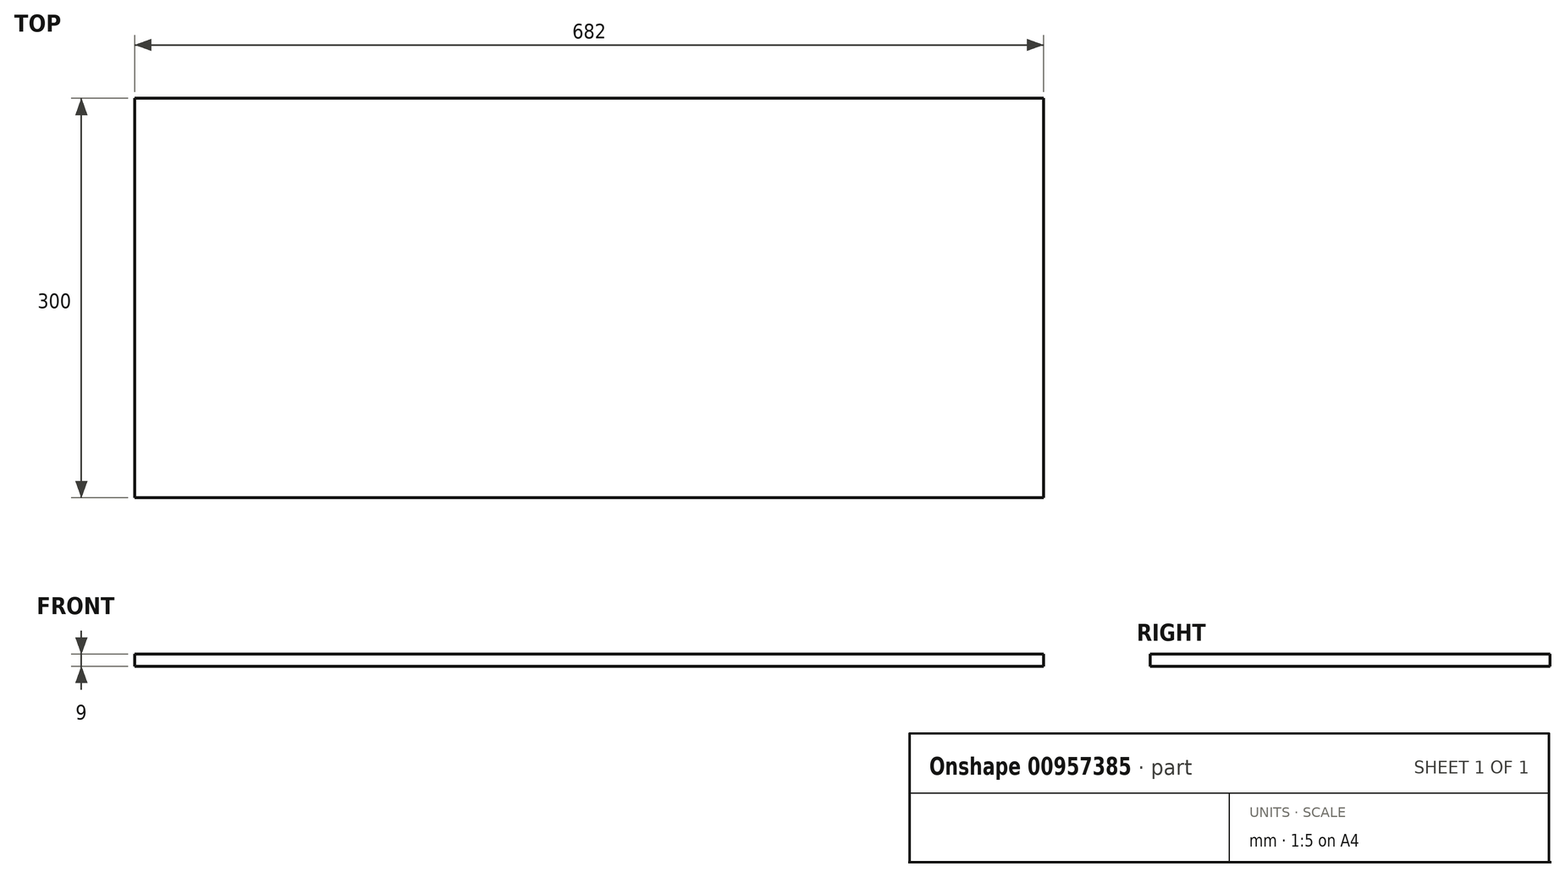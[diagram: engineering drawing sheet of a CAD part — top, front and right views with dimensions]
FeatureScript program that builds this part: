
annotation { "Feature Type Name" : "Feature", "Feature Type Description" : "" }
export const myFeature = defineFeature(function(context is Context, id is Id, definition is map)
    precondition{}
    {
        {
            var Q0;
            Q0=qCreatedBy(makeId("Top.planeOp"),FACE);
            var sketch = newSketch(context, id + "F0", { "sketchPlane" : qUnion([Q0])});
            skLineSegment(sketch, "E0.bottom", {"start": v(341, 150) * mm, "end": v(-341, 150) * mm});
            skLineSegment(sketch, "E0.top", {"start": v(341, -150) * mm, "end": v(-341, -150) * mm});
            skLineSegment(sketch, "E0.left", {"start": v(341, 150) * mm, "end": v(341, -150) * mm});
            skLineSegment(sketch, "E0.right", {"start": v(-341, 150) * mm, "end": v(-341, -150) * mm});
            skPoint(sketch, "E0.middle", {"position": v(0, 0) * mm});
            skSolve(sketch);
        }
        {
            var Q0;
            Q0=makeQuery(id+"F0.imprint","IMPRINT",FACE,{"disambiguationData":[TD([[makeQuery(id+"F0.imprint","IMPRINT",EDGE,{"derivedFrom":sQuery(id+"F0.wireOp",EDGE,"E0.bottom")}),1.0]])]});
            extrude(context, id + "F1", {"entities" : qUnion([Q0]), "depth" : 9 * mm, "offsetDistance" : 25 * mm});
        }
    });
